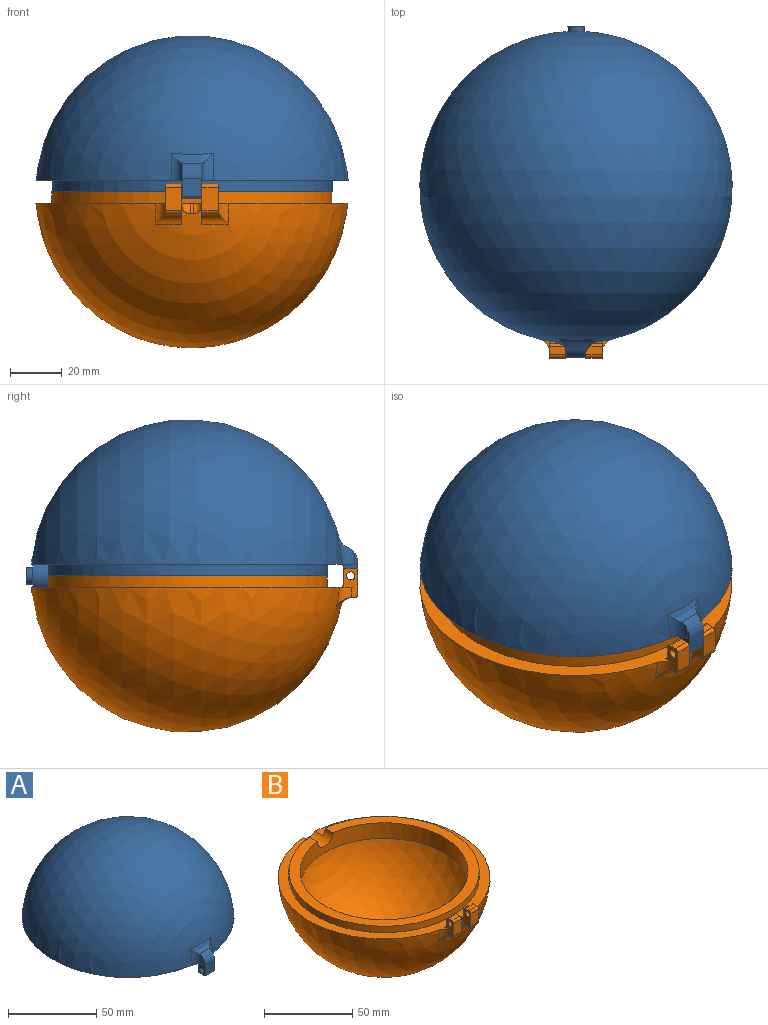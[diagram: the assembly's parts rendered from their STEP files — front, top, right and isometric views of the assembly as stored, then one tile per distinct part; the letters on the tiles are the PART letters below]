
ASSEMBLY  parts=2 mates=1
PART A: 27 faces, bbox 120.4x130.9x66.8 mm
  f0: plane 124.75x120.43mm, normal (0,0,-1), area 2161.2mm2, adj f1,f2,f7,f8,f15,f17,f19,f20
  f1: cylinder r=53.98mm len=107.95mm, axis (0,0,1), area 1459mm2, adj f0,f3,f21
  f2: sphere r=60.32mm, area 20981.4mm2, adj f0,f17,f18,f19,f20
  f3: plane 107.95x107.58mm, normal (0,0,-1), area 1946mm2, adj f1,f6,f21,f25
  f4: sphere r=53.98mm, area 14642.8mm2, adj f5
  f5: plane 105.77x105.77mm, normal (0,0,1), area 1660.7mm2, adj f4,f6
  f6: cylinder r=47.62mm len=95.25mm, axis (0,0,1), area 3166.8mm2, adj f3,f5,f25
  f7: plane 11.79x6.86mm, normal (1,0,0), area 35.2mm2, adj f0,f9,f10,f11,f12,f13,f14,f15
  f8: plane 11.79x6.86mm, normal (-1,0,0), area 35.2mm2, adj f0,f9,f10,f11,f12,f13,f14,f15
  f9: cylinder r=6.35mm len=8.54mm, axis (-1,0,0), area 59.2mm2, adj f7,f8,f10,f17,f18,f19
  f10: plane 7.49x6.92mm, normal (0,-1,0), area 51.9mm2, adj f7,f8,f9,f11
  f11: cylinder r=0.64mm len=7.49mm, axis (-1,0,0), area 7.5mm2, adj f7,f8,f10,f12
  f12: plane 7.49x4.32mm, normal (0,0,-1), area 32.4mm2, adj f7,f8,f11,f13
  f13: cylinder r=0.64mm len=7.49mm, axis (-1,0,0), area 7.5mm2, adj f7,f8,f12,f14
  f14: plane 7.49x5.02mm, normal (0,1,0), area 37.6mm2, adj f7,f8,f13,f15
  f15: cylinder r=1.27mm len=7.49mm, axis (-1,0,0), area 14.9mm2, adj f0,f7,f8,f14
  f16: cylinder r=1.59mm len=7.49mm, axis (-1,0,0), area 74.7mm2, adj f7,f8
  f17: torus R=64.81mm, axis (1,0,0), area 56mm2, adj f0,f2,f8,f9,f18
  f18: bspline ~23.14x4.24mm, area 62mm2, adj f2,f9,f17,f19
  f19: torus R=64.81mm, axis (1,0,0), area 56mm2, adj f0,f2,f7,f9,f18
  f20: cylinder r=6.35mm len=9.07mm, axis (0,-1,0), area 3mm2, adj f0,f2,f22
  f21: cylinder r=6.35mm len=12.7mm, axis (0,-1,0), area 236.4mm2, adj f0,f1,f3,f22,f26
  f22: plane 12.7x12.7mm, normal (0,1,0), area 95mm2, adj f20,f21,f23
  f23: cylinder r=3.17mm len=6.35mm, axis (0,-1,0), area 50.7mm2, adj f22,f24
  f24: plane 6.35x6.35mm, normal (0,1,0), area 31.7mm2, adj f23
  f25: cylinder r=6.35mm len=12.7mm, axis (0,-1,0), area 71.8mm2, adj f3,f6,f26
  f26: plane 12.7x12.7mm, normal (0,-1,0), area 126.7mm2, adj f21,f25
PART B: 40 faces, bbox 121.2x128.7x64.3 mm
  f0: plane 6.29x4.92mm, normal (0,1,0), area 30.9mm2, adj f7,f8,f17,f28
  f1: plane 6.29x3.05mm, normal (0,0,1), area 19.2mm2, adj f8,f9,f17,f28
  f2: cylinder r=1.59mm len=6.29mm, axis (-1,0,0), area 62.7mm2, adj f17,f28
  f3: plane 8.87x6.29mm, normal (0,-1,0), area 55.7mm2, adj f5,f9,f17,f28
  f4: plane 124.36x121.24mm, normal (0,0,1), area 2123.2mm2, adj f7,f14,f15,f16,f17,f20,f28,f29
  f5: cylinder r=1.27mm len=6.29mm, axis (-1,0,0), area 12.5mm2, adj f3,f6,f17,f28
  f6: plane 6.29x1.29mm, normal (0,0,-1), area 5.6mm2, adj f5,f17,f28,f38
  f7: cylinder r=1.27mm len=6.29mm, axis (-1,0,0), area 12.5mm2, adj f0,f4,f17,f28
  f8: cylinder r=1.27mm len=6.29mm, axis (-1,0,0), area 12.5mm2, adj f0,f1,f17,f28
  f9: cylinder r=1.27mm len=6.29mm, axis (-1,0,0), area 12.5mm2, adj f1,f3,f17,f28
  f10: cylinder r=47.62mm len=95.25mm, axis (0,0,1), area 3166.8mm2, adj f12,f13,f39
  f11: sphere r=53.98mm, area 14642.6mm2, adj f12
  f12: plane 105.77x105.77mm, normal (0,0,-1), area 1660.7mm2, adj f10,f11
  f13: plane 107.95x107.58mm, normal (0,0,1), area 1946mm2, adj f10,f15,f39
  f14: sphere r=60.32mm, area 20973.8mm2, adj f4,f27,f28,f29,f32,f34,f35,f36
  f15: cylinder r=53.98mm len=107.95mm, axis (0,0,1), area 1455.9mm2, adj f4,f13,f39
  f16: plane 11.41x6.86mm, normal (1,0,0), area 42.9mm2, adj f4,f18,f19,f20,f21,f22,f23,f24
  f17: plane 11.41x6.86mm, normal (-1,0,0), area 42.9mm2, adj f0,f1,f2,f3,f4,f5,f6,f7
  f18: cylinder r=1.27mm len=6.29mm, axis (-1,0,0), area 12.5mm2, adj f16,f19,f26,f29
  f19: plane 6.29x1.29mm, normal (0,0,-1), area 5.6mm2, adj f16,f18,f29,f36
  f20: cylinder r=1.27mm len=6.29mm, axis (-1,0,0), area 12.5mm2, adj f4,f16,f21,f29
  f21: plane 6.29x4.92mm, normal (0,1,0), area 30.9mm2, adj f16,f20,f22,f29
  f22: cylinder r=1.27mm len=6.29mm, axis (-1,0,0), area 12.5mm2, adj f16,f21,f23,f29
  f23: plane 6.29x3.05mm, normal (0,0,1), area 19.2mm2, adj f16,f22,f24,f29
  f24: cylinder r=1.27mm len=6.29mm, axis (-1,0,0), area 12.5mm2, adj f16,f23,f26,f29
  f25: cylinder r=1.59mm len=6.29mm, axis (-1,0,0), area 62.7mm2, adj f16,f29
  f26: plane 8.87x6.29mm, normal (0,-1,0), area 55.7mm2, adj f16,f18,f24,f29
  f27: plane 1.46x0.22mm, normal (0,0,1), area 0.2mm2, adj f14,f30,f32,f34
  f28: plane 15.52x7.5mm, normal (1,0,0), area 60.9mm2, adj f0,f1,f2,f3,f4,f5,f6,f7
  f29: plane 15.52x7.5mm, normal (-1,0,0), area 60.9mm2, adj f4,f14,f18,f19,f20,f21,f22,f23
  f30: cylinder r=4.57mm len=4.53mm, axis (-1,0,0), area 9.2mm2, adj f4,f27,f31,f33
  f31: torus R=1.4mm, axis (1,0,0), area 22.1mm2, adj f4,f28,f30,f32
  f32: cylinder r=3.17mm len=3.18mm, axis (0,1,0), area 1.4mm2, adj f14,f27,f28,f31
  f33: torus R=1.4mm, axis (1,0,0), area 22.1mm2, adj f4,f29,f30,f34
  f34: cylinder r=3.17mm len=3.18mm, axis (0,-1,0), area 1.4mm2, adj f14,f27,f29,f33
  f35: torus R=63.6mm, axis (1,0,0), area 37.2mm2, adj f4,f14,f16,f36
  f36: torus R=64mm, axis (0,0,1), area 53.6mm2, adj f14,f16,f19,f29,f35
  f37: torus R=63.6mm, axis (1,0,0), area 37.2mm2, adj f4,f14,f17,f38
  f38: torus R=64mm, axis (0,0,1), area 53.6mm2, adj f6,f14,f17,f28,f37
  f39: cylinder r=6.35mm len=12.79mm, axis (0,-1,0), area 193.1mm2, adj f4,f10,f13,f14,f15
PLACE A t=(56.75,20.48,6.01)mm
PLACE B t=(56.62,20.48,6.01)mm
MATE cylindrical A.f16 <-> B.f2  axis (1,0,0) through (60.5,-42.48,6.01)mm
